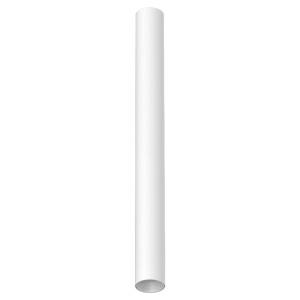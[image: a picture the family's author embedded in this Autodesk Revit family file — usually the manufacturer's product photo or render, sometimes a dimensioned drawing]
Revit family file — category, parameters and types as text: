
# Revit family: hangover_plug_decor_o30_l300__810-0386
name_source: partatom
category: Leuchten
revit_build: Autodesk Revit 2016 (Build: 20190508_0715(x64)
units: mm (PartAtom-declared; Revit-internal decimal feet)

## family parameters
Basisbauteil = Fläche
Beim Laden mit Abzugskörper schneiden = Nein
Bemaßung runder Anschluss = Durchmesser verwenden
Gemeinsam genutzt = Nein
Lichtquelle = Nein
Raumberechnungspunkt = Nein
Teiletyp = Normal

## types (1)
- 810-0386-
    Beschreibung = With 2 powder coated options 841 colour combinations can be achieved. The integrated ballast allows for an operation with.
    Height = 300 mm
    Hersteller = Prolicht
    Lampe = 0 x
    Length = 28 mm
    Luminous efficacy = 0 lm/W
    ModVariant = Nein
    Modell = 810-0386
    Number of Poles = 1
    OnlyDefault = Ja
    Power Factor = 1
    Product Name = HANGOVER PLUG DECOR Ø30 L300
    Product group = Luminaires
    ProductGroupID = 0
    Protection Class = Protection class
    Protection Degree = Degree of protection
    RLX_Detail_Level = 1
    RlxData = <blob elided: 38789 chars, md5=fae979df>
    Scheinlast = 0 VA
    Standby Power = 0 W
    System Light Flux = 0 lm
    System Power = 0 W
    Typenbild = 810-0386.jpg
    URL = http://relux.com
    VarID = 810-0386-
    Voltage = 0 V
    Vorgabe-Ansicht = 1800 mm
    Weight = 0.00 kg
    Width = 0 mm  [stored 0 ft]

note: [stored X ft] marks values corroborated as IEEE doubles in the binary element streams (Revit-internal decimal feet)

## geometry (parser evidence)
native form markers: Sweep x10
no freeform markers — native parametric forms only
